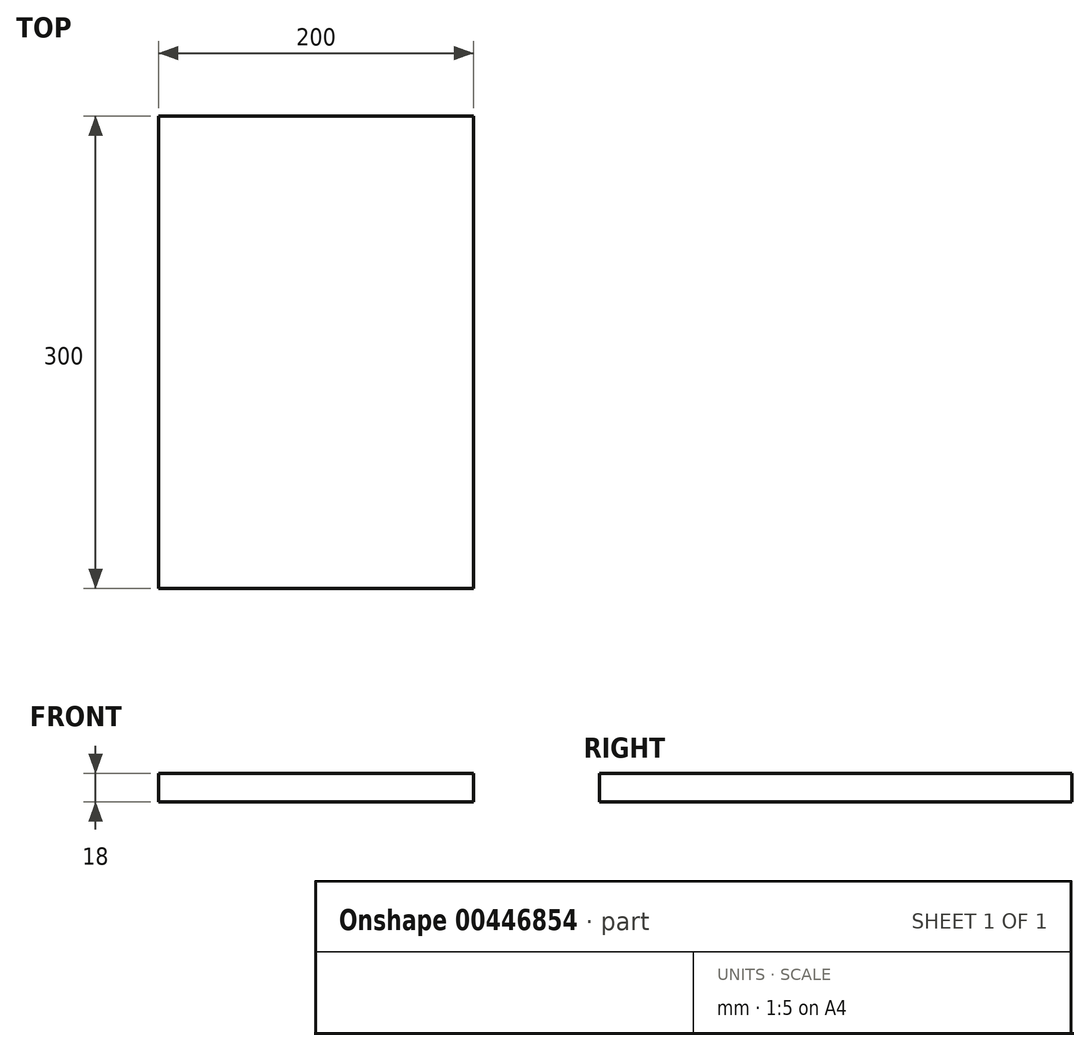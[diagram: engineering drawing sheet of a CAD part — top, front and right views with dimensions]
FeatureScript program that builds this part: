
annotation { "Feature Type Name" : "Feature", "Feature Type Description" : "" }
export const myFeature = defineFeature(function(context is Context, id is Id, definition is map)
    precondition{}
    {
        {
            var Q0;
            Q0=qCreatedBy(makeId("Top.planeOp"),FACE);
            var sketch = newSketch(context, id + "F0", { "sketchPlane" : qUnion([Q0])});
            skLineSegment(sketch, "E0.bottom", {"start": v(0, 0) * mm, "end": v(200, 0) * mm});
            skLineSegment(sketch, "E0.top", {"start": v(0, 300) * mm, "end": v(200, 300) * mm});
            skLineSegment(sketch, "E0.left", {"start": v(0, 0) * mm, "end": v(0, 300) * mm});
            skLineSegment(sketch, "E0.right", {"start": v(200, 0) * mm, "end": v(200, 300) * mm});
            skSolve(sketch);
        }
        {
            var Q0;
            Q0=makeQuery(id+"F0.imprint","IMPRINT",FACE,{"disambiguationData":[TD([[makeQuery(id+"F0.imprint","IMPRINT",EDGE,{"derivedFrom":sQuery(id+"F0.wireOp",EDGE,"E0.bottom")}),1.0]])]});
            extrude(context, id + "F1", {"entities" : qUnion([Q0]), "depth" : 18 * mm});
        }
    });
